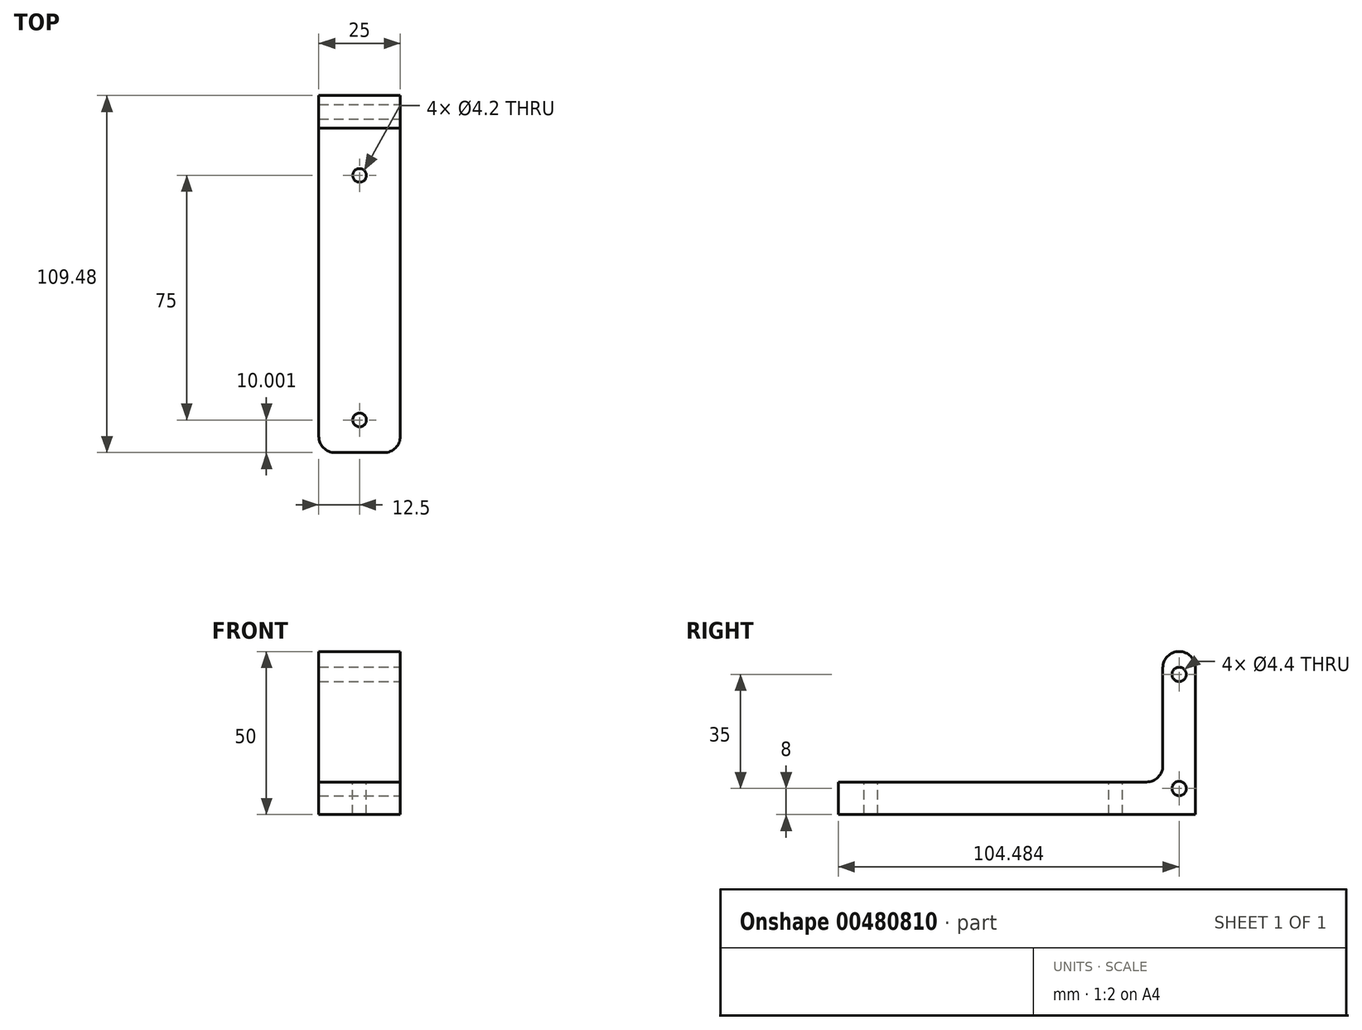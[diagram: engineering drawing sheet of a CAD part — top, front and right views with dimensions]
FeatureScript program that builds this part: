
annotation { "Feature Type Name" : "Feature", "Feature Type Description" : "" }
export const myFeature = defineFeature(function(context is Context, id is Id, definition is map)
    precondition{}
    {
        {
            var Q0;
            Q0=qCreatedBy(makeId("Right.planeOp"),FACE);
            var sketch = newSketch(context, id + "F0", { "sketchPlane" : qUnion([Q0])});
            skLineSegment(sketch, "E0", {"start": v(-127.76, 0) * mm, "end": v(-18.28, 0) * mm});
            skLineSegment(sketch, "E1", {"start": v(-18.28, 0) * mm, "end": v(-18.28, 50) * mm});
            skLineSegment(sketch, "E2", {"start": v(-18.28, 50) * mm, "end": v(-28.28, 50) * mm});
            skLineSegment(sketch, "E3", {"start": v(-28.28, 50) * mm, "end": v(-28.28, 10) * mm});
            skLineSegment(sketch, "E4", {"start": v(-28.28, 10) * mm, "end": v(-127.76, 10) * mm});
            skLineSegment(sketch, "E5", {"start": v(-127.76, 10) * mm, "end": v(-127.76, 0) * mm});
            skSolve(sketch);
        }
        {
            var Q0;
            Q0=makeQuery(id+"F0.imprint","IMPRINT",FACE,{"disambiguationData":[TD([[makeQuery(id+"F0.imprint","IMPRINT",EDGE,{"derivedFrom":sQuery(id+"F0.wireOp",EDGE,"E0")}),1.0]])]});
            extrude(context, id + "F1", {"entities" : qUnion([Q0]), "depth" : 25 * mm});
        }
        {
            var Q0;
            Q0=makeQuery(id+"F1.opExtrude","CAP_FACE",FACE,{"disambiguationData":[OSD([sQuery(id+"F0.wireOp",EDGE,"E0"),sQuery(id+"F0.wireOp",EDGE,"E1"),sQuery(id+"F0.wireOp",EDGE,"E2"),sQuery(id+"F0.wireOp",EDGE,"E3"),sQuery(id+"F0.wireOp",EDGE,"E4"),sQuery(id+"F0.wireOp",EDGE,"E5")])],"isStart":false});
            cPlane(context, id + "F2", {"entities" : qUnion([Q0]), "cplaneType" : CPlaneType.OFFSET, "offset" : (25 / 2) * mm, "oppositeDirection" : true, "width" : 150 * mm, "height" : 150 * mm});
        }
        {
            var Q0;
            Q0=makeQuery(id+"F1.opExtrude","SWEPT_FACE",FACE,{"disambiguationData":[OSD([sQuery(id+"F0.wireOp",EDGE,"E4")])]});
            var sketch = newSketch(context, id + "F3", { "sketchPlane" : qUnion([Q0])});
            skCircle(sketch, "E6", {"center": v(12.5, -117.76) * mm, "radius": 2.1 * mm});
            skCircle(sketch, "E7", {"center": v(12.5, -42.76) * mm, "radius": 2.1 * mm});
            skSolve(sketch);
        }
        {
            var Q0;
            Q0=makeQuery(id+"F3.imprint","IMPRINT",FACE,{"disambiguationData":[TD([[makeQuery(id+"F3.imprint","IMPRINT",EDGE,{"derivedFrom":sQuery(id+"F3.wireOp",EDGE,"E6")}),1.0]])]});
            var Q1;
            Q1=makeQuery(id+"F3.imprint","IMPRINT",FACE,{"disambiguationData":[TD([[makeQuery(id+"F3.imprint","IMPRINT",EDGE,{"derivedFrom":sQuery(id+"F3.wireOp",EDGE,"E7")}),1.0]])]});
            extrude(context, id + "F4", {"entities" : qUnion([Q0, Q1]), "operationType" : NewBodyOperationType.REMOVE, "oppositeDirection" : true, "depth" : 25 * mm});
        }
        {
            var Q0;
            Q0=makeQuery(id+"F1.opExtrude","SWEPT_FACE",FACE,{"disambiguationData":[OSD([sQuery(id+"F0.wireOp",EDGE,"E3")])]});
            cPlane(context, id + "F5", {"entities" : qUnion([Q0]), "cplaneType" : CPlaneType.OFFSET, "offset" : 5 * mm, "oppositeDirection" : true, "width" : 150 * mm, "height" : 150 * mm});
        }
        {
            var Q0;
            Q0=makeQuery(id+"F1.opExtrude","CAP_FACE",FACE,{"disambiguationData":[OSD([sQuery(id+"F0.wireOp",EDGE,"E0"),sQuery(id+"F0.wireOp",EDGE,"E1"),sQuery(id+"F0.wireOp",EDGE,"E2"),sQuery(id+"F0.wireOp",EDGE,"E3"),sQuery(id+"F0.wireOp",EDGE,"E4"),sQuery(id+"F0.wireOp",EDGE,"E5")])],"isStart":false});
            var sketch = newSketch(context, id + "F6", { "sketchPlane" : qUnion([Q0])});
            skCircle(sketch, "E8", {"center": v(-23.28, 43) * mm, "radius": 2.2 * mm});
            skCircle(sketch, "E9", {"center": v(-23.28, 8) * mm, "radius": 2.2 * mm});
            skSolve(sketch);
        }
        {
            var Q0;
            Q0 = qSketchRegion(id + "F6", true);
            extrude(context, id + "F7", {"entities" : qUnion([Q0]), "operationType" : NewBodyOperationType.REMOVE, "oppositeDirection" : true, "depth" : 25 * mm});
        }
        {
            var Q0;
            Q0=makeQuery(id+"F1.opExtrude","SWEPT_EDGE",EDGE,{"disambiguationData":[OSD([sQuery(id+"F0.wireOp",EDGE,"E3"),sQuery(id+"F0.wireOp",EDGE,"E4")])]});
            var Q1;
            Q1=makeQuery(id+"F1.opExtrude","SWEPT_EDGE",EDGE,{"disambiguationData":[OSD([sQuery(id+"F0.wireOp",EDGE,"E1"),sQuery(id+"F0.wireOp",EDGE,"E2")])]});
            var Q2;
            Q2=makeQuery(id+"F1.opExtrude","SWEPT_EDGE",EDGE,{"disambiguationData":[OSD([sQuery(id+"F0.wireOp",EDGE,"E2"),sQuery(id+"F0.wireOp",EDGE,"E3")])]});
            var Q3;
            Q3=makeQuery(id+"F1.opExtrude","CAP_EDGE",EDGE,{"disambiguationData":[OSD([sQuery(id+"F0.wireOp",EDGE,"E5")])],"isStart":false});
            var Q4;
            Q4=makeQuery(id+"F1.opExtrude","CAP_EDGE",EDGE,{"disambiguationData":[OSD([sQuery(id+"F0.wireOp",EDGE,"E5")])],"isStart":true});
            fillet(context, id + "F8", {"entities" : qUnion([Q0, Q1, Q2, Q3, Q4]), "radius" : 5 * mm, "tangentPropagation" : true, "allowEdgeOverflow" : false});
        }
    });
